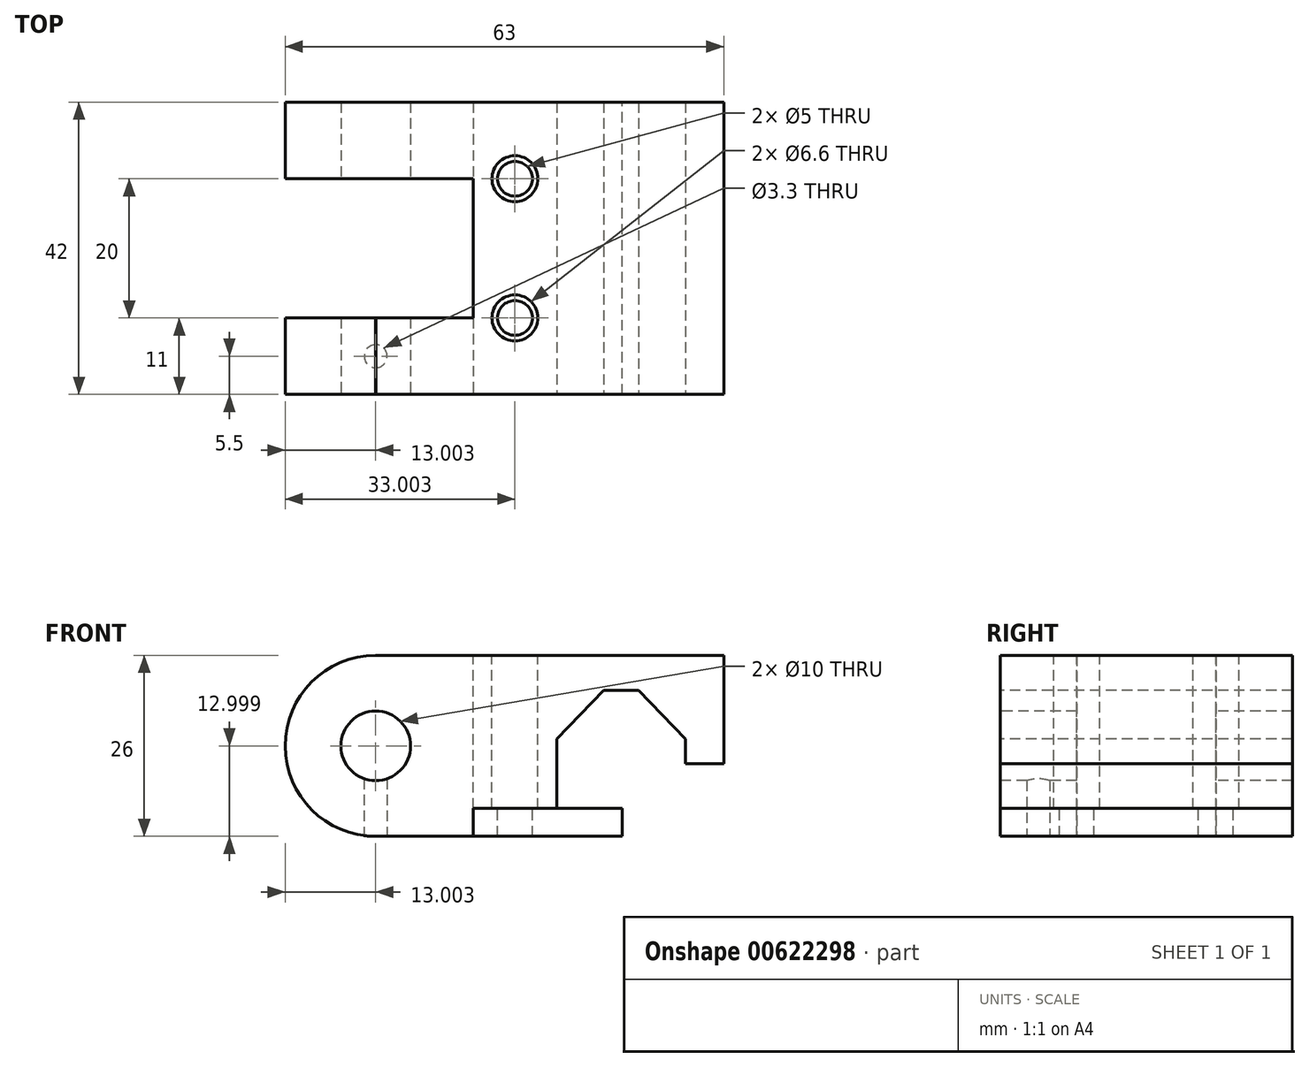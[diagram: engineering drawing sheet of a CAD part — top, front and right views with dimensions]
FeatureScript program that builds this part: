
annotation { "Feature Type Name" : "Feature", "Feature Type Description" : "" }
export const myFeature = defineFeature(function(context is Context, id is Id, definition is map)
    precondition{}
    {
        {
            var Q0;
            Q0=qCreatedBy(makeId("Front.planeOp"),FACE);
            var sketch = newSketch(context, id + "F0", { "sketchPlane" : qUnion([Q0])});
            skLineSegment(sketch, "E0", {"start": v(10.4, 7.7) * mm, "end": v(15.4, 7.7) * mm});
            skLineSegment(sketch, "E1", {"start": v(15.4, 7.7) * mm, "end": v(22.14, 0.7) * mm});
            skLineSegment(sketch, "E2", {"start": v(-22.36, 12.7) * mm, "end": v(27.64, 12.7) * mm});
            skLineSegment(sketch, "E3", {"start": v(-8.36, -13.3) * mm, "end": v(-22.36, -13.3) * mm});
            skLineSegment(sketch, "E4", {"start": v(22.14, -2.88) * mm, "end": v(27.64, -2.88) * mm});
            skLineSegment(sketch, "E5", {"start": v(22.14, -2.88) * mm, "end": v(22.14, 0.7) * mm});
            skLineSegment(sketch, "E6", {"start": v(10.4, 7.7) * mm, "end": v(3.64, 0.7) * mm});
            skLineSegment(sketch, "E7", {"start": v(3.64, 0.7) * mm, "end": v(3.64, -9.3) * mm});
            skLineSegment(sketch, "E8", {"start": v(27.64, -2.88) * mm, "end": v(27.64, 12.7) * mm});
            skLineSegment(sketch, "E9", {"start": v(-22.36, 18.7) * mm, "end": v(-22.36, -23.6) * mm, "construction": true});
            skLineSegment(sketch, "E10", {"start": v(-33.44, -0.3) * mm, "end": v(-7.35, -0.3) * mm, "construction": true});
            skCircle(sketch, "E11", {"center": v(-22.36, -0.3) * mm, "radius": 5 * mm});
            skArc(sketch, "E12", {"start": v(-22.36, 12.7) * mm, "mid": v(-35.36, -0.3) * mm, "end": v(-22.36, -13.3) * mm});
            skPoint(sketch, "E13.orphan", {"position": v(-36.36, -13.3) * mm});
            skLineSegment(sketch, "E14", {"start": v(-8.36, -9.3) * mm, "end": v(3.64, -9.3) * mm});
            skLineSegment(sketch, "E15", {"start": v(-8.36, -9.3) * mm, "end": v(-8.36, -13.3) * mm});
            skLineSegment(sketch, "E16", {"start": v(-2.36, -9.3) * mm, "end": v(-2.36, 20.11) * mm, "construction": true});
            skSolve(sketch);
        }
        {
            var Q0;
            Q0=makeQuery(id+"F0.imprint","IMPRINT",FACE,{"disambiguationData":[TD([[makeQuery(id+"F0.imprint","IMPRINT",EDGE,{"derivedFrom":sQuery(id+"F0.wireOp",EDGE,"E0")}),1.0]])]});
            extrude(context, id + "F1", {"entities" : qUnion([Q0]), "oppositeDirection" : true, "depth" : 42 * mm});
        }
        {
            var Q0;
            Q0=makeQuery(id+"F1.opExtrude","SWEPT_FACE",FACE,{"disambiguationData":[OSD([sQuery(id+"F0.wireOp",EDGE,"E2")])]});
            var sketch = newSketch(context, id + "F2", { "sketchPlane" : qUnion([Q0])});
            skLineSegment(sketch, "E17", {"start": v(-37.57, 31) * mm, "end": v(-8.36, 31) * mm});
            skLineSegment(sketch, "E18", {"start": v(-37.48, 11) * mm, "end": v(-8.36, 11) * mm});
            skLineSegment(sketch, "E19", {"start": v(-8.36, 31) * mm, "end": v(-8.36, 11) * mm});
            skLineSegment(sketch, "E20", {"start": v(-37.57, 31) * mm, "end": v(-37.48, 11) * mm});
            skSolve(sketch);
        }
        {
            var Q0;
            {var subQ0=sQuery(id+"F2.wireOp",EDGE,"E20");Q0=makeQuery(id+"F2.imprint","IMPRINT",FACE,{"disambiguationData":[TD([[makeQuery(id+"F2.imprint","IMPRINT",EDGE,{"derivedFrom":subQ0}),1.0]])]});}
            var Q1;
            {var subQ0=sQuery(id+"F2.wireOp",EDGE,"E19");Q1=makeQuery(id+"F2.imprint","IMPRINT",FACE,{"disambiguationData":[TD([[makeQuery(id+"F2.imprint","IMPRINT",EDGE,{"derivedFrom":subQ0}),-1.0]])]});}
            extrude(context, id + "F3", {"entities" : qUnion([Q0, Q1]), "operationType" : NewBodyOperationType.REMOVE, "endBound" : BoundingType.THROUGH_ALL, "oppositeDirection" : true, "depth" : 25 * mm});
        }
        {
            var Q0;
            Q0=makeQuery(id+"F1.opExtrude","SWEPT_FACE",FACE,{"disambiguationData":[OSD([sQuery(id+"F0.wireOp",EDGE,"E3")])]});
            var sketch = newSketch(context, id + "F4", { "sketchPlane" : qUnion([Q0])});
            skPoint(sketch, "E21", {"position": v(-22.36, -5.5) * mm});
            skSolve(sketch);
        }
        {
            var Q0;
            Q0=sQuery(id+"F4.wireOp",VERTEX,"E21");
            var Q1;
            Q1=makeQuery(id+"F1.opExtrude","SWEPT_BODY",BODY,{"disambiguationData":[OSD([sQuery(id+"F0.wireOp",EDGE,"E0"),sQuery(id+"F0.wireOp",EDGE,"E1"),sQuery(id+"F0.wireOp",EDGE,"E2"),sQuery(id+"F0.wireOp",EDGE,"E3"),sQuery(id+"F0.wireOp",EDGE,"E4"),sQuery(id+"F0.wireOp",EDGE,"E5"),sQuery(id+"F0.wireOp",EDGE,"E6"),sQuery(id+"F0.wireOp",EDGE,"E7"),sQuery(id+"F0.wireOp",EDGE,"E8"),sQuery(id+"F0.wireOp",EDGE,"E11"),sQuery(id+"F0.wireOp",EDGE,"E12")])]});
            hole(context, id + "F5", {"style" : HoleStyle.SIMPLE, "endStyle" : HoleEndStyle.BLIND, "standardTappedOrClearance" : lookupTablePath({ "standard" : "ISO", "fit" : "Normal", "size" : "M3", "type" : "Clearance" }), "standardBlindInLast" : lookupTablePath({ "fit" : "Standard", "standard" : "ISO", "size" : "M3", "type" : "Clearance" }), "holeDiameter" : 3.3 * mm, "holeDepth" : 9 * mm, "locations" : qUnion([Q0]), "scope" : qUnion([Q1])});
        }
        {
            var Q0;
            Q0=makeQuery(id+"F1.opExtrude","SWEPT_FACE",FACE,{"disambiguationData":[OSD([sQuery(id+"F0.wireOp",EDGE,"E2")])]});
            var sketch = newSketch(context, id + "F6", { "sketchPlane" : qUnion([Q0])});
            skPoint(sketch, "E22", {"position": v(-2.36, 31) * mm});
            skPoint(sketch, "E23", {"position": v(-2.36, 11) * mm});
            skSolve(sketch);
        }
        {
            var Q0;
            Q0=sQuery(id+"F6.wireOp",VERTEX,"E22");
            var Q1;
            Q1=sQuery(id+"F6.wireOp",VERTEX,"E23");
            var Q2;
            Q2=makeQuery(id+"F1.opExtrude","SWEPT_BODY",BODY,{"disambiguationData":[OSD([sQuery(id+"F0.wireOp",EDGE,"E0"),sQuery(id+"F0.wireOp",EDGE,"E1"),sQuery(id+"F0.wireOp",EDGE,"E2"),sQuery(id+"F0.wireOp",EDGE,"E3"),sQuery(id+"F0.wireOp",EDGE,"E4"),sQuery(id+"F0.wireOp",EDGE,"E5"),sQuery(id+"F0.wireOp",EDGE,"E6"),sQuery(id+"F0.wireOp",EDGE,"E7"),sQuery(id+"F0.wireOp",EDGE,"E8"),sQuery(id+"F0.wireOp",EDGE,"E11"),sQuery(id+"F0.wireOp",EDGE,"E12"),sQuery(id+"F0.wireOp",EDGE,"E14"),sQuery(id+"F0.wireOp",EDGE,"E15")])]});
            hole(context, id + "F7", {"style" : HoleStyle.SIMPLE, "endStyle" : HoleEndStyle.THROUGH, "standardTappedOrClearance" : lookupTablePath({ "standard" : "ISO", "fit" : "Normal", "size" : "M6", "type" : "Clearance" }), "standardBlindInLast" : lookupTablePath({ "fit" : "Standard", "standard" : "ISO", "size" : "M6", "type" : "Clearance" }), "holeDiameter" : 6.6 * mm, "locations" : qUnion([Q0, Q1]), "scope" : qUnion([Q2]), "isTappedThrough" : true});
        }
        {
            var Q0;
            Q0=makeQuery(id+"F1.opExtrude","SWEPT_FACE",FACE,{"disambiguationData":[OSD([sQuery(id+"F0.wireOp",EDGE,"E14")])]});
            var sketch = newSketch(context, id + "F8", { "sketchPlane" : qUnion([Q0])});
            skLineSegment(sketch, "E24.bottom", {"start": v(-8.36, 0) * mm, "end": v(13.06, 0) * mm});
            skLineSegment(sketch, "E24.top", {"start": v(-8.36, -42) * mm, "end": v(13.06, -42) * mm});
            skLineSegment(sketch, "E24.left", {"start": v(-8.36, 0) * mm, "end": v(-8.36, -42) * mm});
            skLineSegment(sketch, "E24.right", {"start": v(13.06, 0) * mm, "end": v(13.06, -42) * mm});
            skSolve(sketch);
        }
        {
            var Q0;
            Q0=qSketchRegion(id+"F8",true);
            var Q1;
            {var subQ1=makeQuery(id+"F1.opExtrude","SWEPT_EDGE",EDGE,{"disambiguationData":[OSD([sQuery(id+"F0.wireOp",EDGE,"E7"),sQuery(id+"F0.wireOp",EDGE,"E14")])]});Q1=makeQuery(id+"F8.imprint","IMPRINT",FACE,{"disambiguationData":[TD([[makeQuery(id+"F8.imprint","IMPRINT",EDGE,{"derivedFrom":subQ1}),1.0]])]});}
            extrude(context, id + "F9", {"entities" : qUnion([Q0, Q1]), "depth" : 4 * mm});
        }
        {
            var Q0;
            Q0=sQuery(id+"F6.wireOp",VERTEX,"E23");
            var Q1;
            Q1=sQuery(id+"F6.wireOp",VERTEX,"E22");
            var Q2;
            Q2=makeQuery(id+"F9.opExtrude","SWEPT_BODY",BODY,{"disambiguationData":[OSD([sQuery(id+"F8.wireOp",EDGE,"E24.bottom"),sQuery(id+"F8.wireOp",EDGE,"E24.top"),sQuery(id+"F8.wireOp",EDGE,"E24.left"),sQuery(id+"F8.wireOp",EDGE,"E24.right")])]});
            hole(context, id + "F10", {"style" : HoleStyle.SIMPLE, "endStyle" : HoleEndStyle.THROUGH, "standardTappedOrClearance" : lookupTablePath({ "standard" : "ISO", "engagement" : "75%", "pitch" : "1 mm", "size" : "M6", "type" : "Tapped" }), "standardBlindInLast" : lookupTablePath({ "standard" : "ISO", "engagement" : "75%", "pitch" : "1 mm", "size" : "M6", "type" : "Tapped" }), "holeDiameter" : 5 * mm, "locations" : qUnion([Q0, Q1]), "scope" : qUnion([Q2]), "isTappedThrough" : true, "majorDiameter" : 6 * mm, "showTappedDepth" : true});
        }
        {
            var Q0;
            Q0=makeQuery(id+"F1.opExtrude","CAP_FACE",FACE,{"disambiguationData":[OSD([sQuery(id+"F0.wireOp",EDGE,"E0"),sQuery(id+"F0.wireOp",EDGE,"E1"),sQuery(id+"F0.wireOp",EDGE,"E2"),sQuery(id+"F0.wireOp",EDGE,"E3"),sQuery(id+"F0.wireOp",EDGE,"E4"),sQuery(id+"F0.wireOp",EDGE,"E5"),sQuery(id+"F0.wireOp",EDGE,"E6"),sQuery(id+"F0.wireOp",EDGE,"E7"),sQuery(id+"F0.wireOp",EDGE,"E8"),sQuery(id+"F0.wireOp",EDGE,"E11"),sQuery(id+"F0.wireOp",EDGE,"E12"),sQuery(id+"F0.wireOp",EDGE,"E14"),sQuery(id+"F0.wireOp",EDGE,"E15")])],"isStart":true});
            var sketch = newSketch(context, id + "F11", { "sketchPlane" : qUnion([Q0])});
            skLineSegment(sketch, "E25", {"start": v(-22.4, 12.7) * mm, "end": v(-22.36, 12.55) * mm});
            skLineSegment(sketch, "E26", {"start": v(-22.36, 12.55) * mm, "end": v(-22.32, 12.7) * mm});
            skLineSegment(sketch, "E27", {"start": v(-22.4, 12.7) * mm, "end": v(-22.32, 12.7) * mm});
            skSolve(sketch);
        }
        {
            var Q0;
            {var subQ0=sQuery(id+"F11.wireOp",EDGE,"E25");Q0=makeQuery(id+"F11.imprint","IMPRINT",FACE,{"disambiguationData":[TD([[makeQuery(id+"F11.imprint","IMPRINT",EDGE,{"derivedFrom":subQ0}),1.0]])]});}
            extrude(context, id + "F12", {"entities" : qUnion([Q0]), "operationType" : NewBodyOperationType.REMOVE, "endBound" : BoundingType.UP_TO_NEXT, "oppositeDirection" : true, "depth" : 25 * mm});
        }
    });
